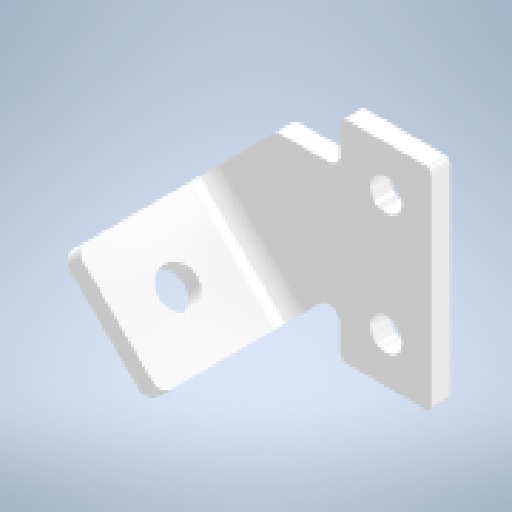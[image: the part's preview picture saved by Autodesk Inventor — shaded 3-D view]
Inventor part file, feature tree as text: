
AUTODESK INVENTOR PART (.ipt)
format: ipt  version: 2024 (Build 280153000, 153)  size: 330,752 bytes
history: native  units: mm
features: sheet_metal_op x4, sketch x3, fillet x3, hole x2, other x2
ambient origin geometry x8: Origin, YZ Plane, XZ Plane, XY Plane, X Axis, Y Axis, Z Axis, Center Point
bodies: Body1 (feature_tree)
feature tree (14):
  sketch  "Sketch1"  dims[d1=28.0mm d2=21.5mm d3=35.0mm d5=20.0mm]
  sheet_metal_op  "Face2"
  sheet_metal_op  "Flange1"
  fillet  "Fillet1"  Radius=30.0mm
  hole  "Hole2"  [1 undecoded]
  fillet  "Fillet2"  Radius=35.0mm
  fillet  "Fillet3"  Radius=20.0mm
  hole  "Hole1"  [1 undecoded]
  other  "Plate2"
  sketch  "Sketch2"  dims[d6=7.5mm d7=7.5mm]
  other  "Plate3"
  sheet_metal_op  "Bend1"
  sheet_metal_op  "Corner1"
  sketch  "Sketch3"  dims[d8=7.5mm d11=20.0mm d12=20.0mm d13=3.175mm d14=3.175mm d15=1.5875mm d16=6.35mm d17=3.175mm d18=25.0mm d19=90.0deg d20=3.175mm d21=12.7mm d22=3.175mm d23=3.175mm d24=2.0mm d25=2.0mm d26=1.0mm d27=5.3mm d28=6.0mm d29=4.0mm d30=2.0mm d31=90.0deg d32=3.175mm d33=20.594885mm d34=6.3mm d35=6.0mm d36=4.0mm d37=2.0mm d38=90.0deg d39=8.0mm d40=20.594885mm]
note: 2 required parameter values undecoded (feature->parameter linkage not recoverable at this tier; creation-order binding heuristic only, values carry confidence <= 0.55)
